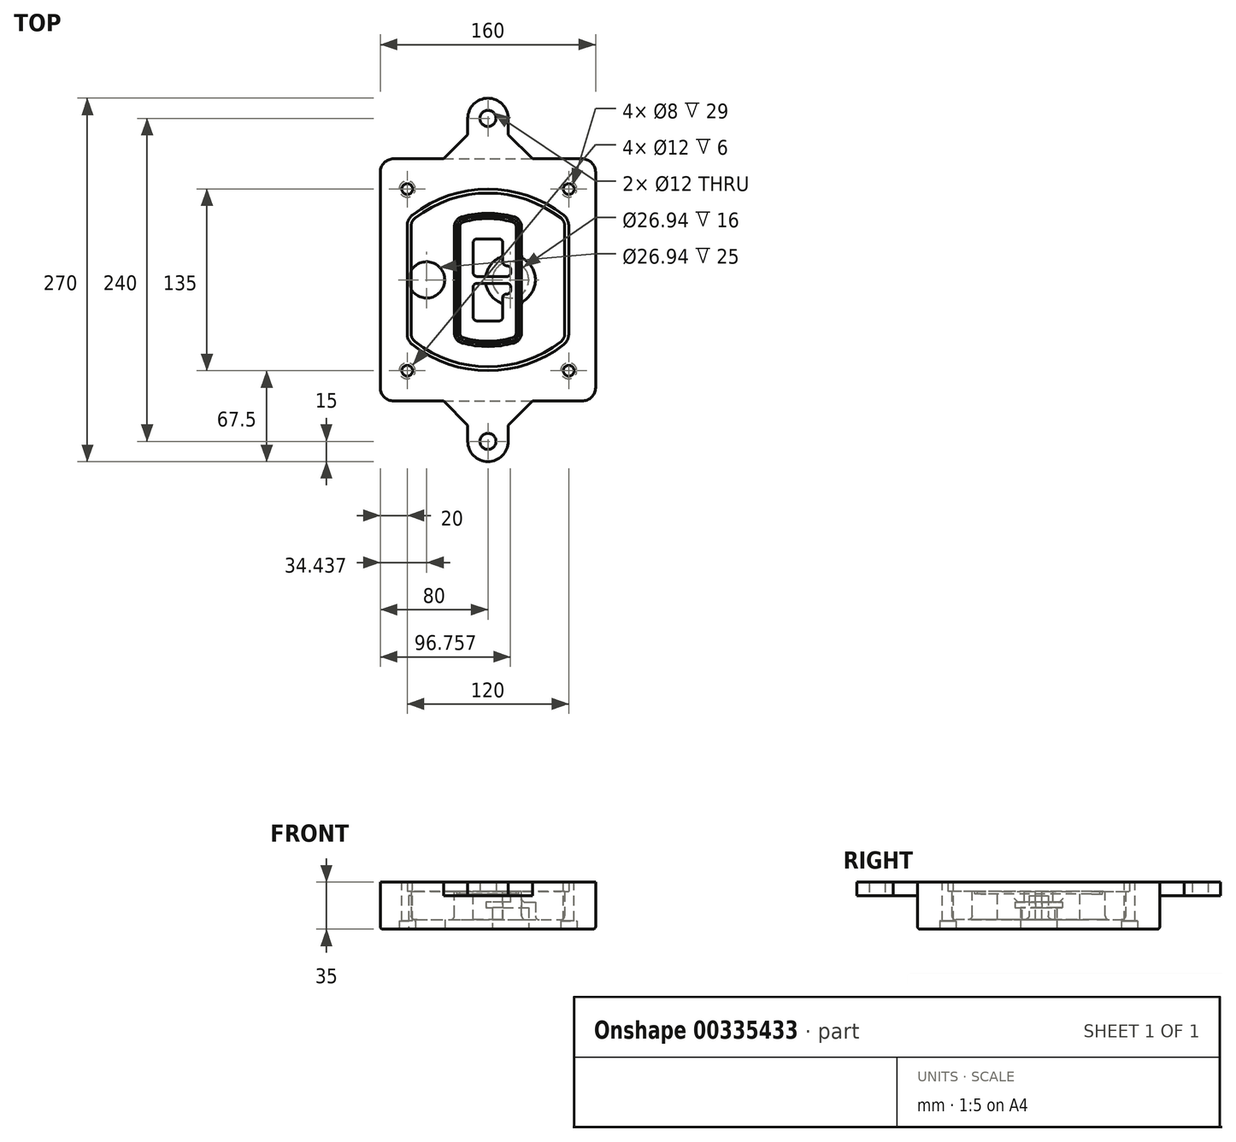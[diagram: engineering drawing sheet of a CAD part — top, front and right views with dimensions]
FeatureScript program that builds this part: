
annotation { "Feature Type Name" : "Feature", "Feature Type Description" : "" }
export const myFeature = defineFeature(function(context is Context, id is Id, definition is map)
    precondition{}
    {
        {
            var Q0;
            Q0=qCreatedBy(makeId("Top.planeOp"),FACE);
            var sketch = newSketch(context, id + "F0", { "sketchPlane" : qUnion([Q0])});
            skPoint(sketch, "E0.rect.middle", {"position": v(0, 0) * mm});
            skLineSegment(sketch, "E1.bottom", {"start": v(-70, -90) * mm, "end": v(70, -90) * mm});
            skLineSegment(sketch, "E1.top", {"start": v(-70, 90) * mm, "end": v(70, 90) * mm});
            skLineSegment(sketch, "E1.left", {"start": v(-80, -80) * mm, "end": v(-80, 80) * mm});
            skLineSegment(sketch, "E1.right", {"start": v(80, -80) * mm, "end": v(80, 80) * mm});
            skLineSegment(sketch, "E2", {"start": v(-80, 90) * mm, "end": v(80, -90) * mm, "construction": true});
            skLineSegment(sketch, "E3", {"start": v(80, 90) * mm, "end": v(-80, -90) * mm, "construction": true});
            skCircle(sketch, "E4", {"center": v(-60, 67.5) * mm, "radius": 4 * mm});
            skCircle(sketch, "E5", {"center": v(60, 67.5) * mm, "radius": 4 * mm});
            skCircle(sketch, "E6", {"center": v(60, -67.5) * mm, "radius": 4 * mm});
            skCircle(sketch, "E7", {"center": v(-60, -67.5) * mm, "radius": 4 * mm});
            skLineSegment(sketch, "E8", {"start": v(-60, 67.5) * mm, "end": v(60, 67.5) * mm, "construction": true});
            skLineSegment(sketch, "E9", {"start": v(60, 67.5) * mm, "end": v(60, -67.5) * mm, "construction": true});
            skLineSegment(sketch, "E10", {"start": v(60, -67.5) * mm, "end": v(-60, -67.5) * mm, "construction": true});
            skLineSegment(sketch, "E11", {"start": v(-60, -67.5) * mm, "end": v(-60, 67.5) * mm, "construction": true});
            skLineSegment(sketch, "E12", {"start": v(-60, 40.3) * mm, "end": v(-60, -40.3) * mm});
            skLineSegment(sketch, "E13", {"start": v(60, 40.3) * mm, "end": v(60, -40.3) * mm});
            skArc(sketch, "E14", {"start": v(56.15, 48.18) * mm, "mid": v(0, 67.5) * mm, "end": v(-56.15, 48.18) * mm});
            skArc(sketch, "E15", {"start": v(-56.15, -48.18) * mm, "mid": v(0, -67.5) * mm, "end": v(56.15, -48.18) * mm});
            skLineSegment(sketch, "E16", {"start": v(-60, 0) * mm, "end": v(60, 0) * mm, "construction": true});
            skPoint(sketch, "E17.visualSharp", {"position": v(-60, -45) * mm});
            skArc(sketch, "E17.filletArc", {"start": v(-60, -40.3) * mm, "mid": v(-58.99, -44.68) * mm, "end": v(-56.15, -48.18) * mm});
            skPoint(sketch, "E18.visualSharp", {"position": v(-60, 45) * mm});
            skArc(sketch, "E18.filletArc", {"start": v(-56.15, 48.18) * mm, "mid": v(-58.99, 44.68) * mm, "end": v(-60, 40.3) * mm});
            skPoint(sketch, "E19.visualSharp", {"position": v(60, 45) * mm});
            skArc(sketch, "E19.filletArc", {"start": v(60, 40.3) * mm, "mid": v(58.99, 44.68) * mm, "end": v(56.15, 48.18) * mm});
            skPoint(sketch, "E20.visualSharp", {"position": v(60, -45) * mm});
            skArc(sketch, "E20.filletArc", {"start": v(56.15, -48.18) * mm, "mid": v(58.99, -44.68) * mm, "end": v(60, -40.3) * mm});
            skPoint(sketch, "E21.visualSharp", {"position": v(-80, 90) * mm});
            skArc(sketch, "E21.filletArc", {"start": v(-70, 90) * mm, "mid": v(-77.07, 87.07) * mm, "end": v(-80, 80) * mm});
            skPoint(sketch, "E22.visualSharp", {"position": v(80, 90) * mm});
            skArc(sketch, "E22.filletArc", {"start": v(80, 80) * mm, "mid": v(77.07, 87.07) * mm, "end": v(70, 90) * mm});
            skPoint(sketch, "E23.visualSharp", {"position": v(80, -90) * mm});
            skArc(sketch, "E23.filletArc", {"start": v(70, -90) * mm, "mid": v(77.07, -87.07) * mm, "end": v(80, -80) * mm});
            skPoint(sketch, "E24.visualSharp", {"position": v(-80, -90) * mm});
            skArc(sketch, "E24.filletArc", {"start": v(-80, -80) * mm, "mid": v(-77.07, -87.07) * mm, "end": v(-70, -90) * mm});
            skArc(sketch, "E25.0", {"start": v(57, 40.3) * mm, "mid": v(56.3, 43.36) * mm, "end": v(54.3, 45.81) * mm});
            skLineSegment(sketch, "E25.1", {"start": v(57, 40.3) * mm, "end": v(57, -40.3) * mm});
            skArc(sketch, "E25.2", {"start": v(54.3, -45.81) * mm, "mid": v(56.3, -43.36) * mm, "end": v(57, -40.3) * mm});
            skArc(sketch, "E25.3", {"start": v(-54.3, -45.81) * mm, "mid": v(0, -64.5) * mm, "end": v(54.3, -45.81) * mm});
            skArc(sketch, "E25.4", {"start": v(-57, -40.3) * mm, "mid": v(-56.3, -43.36) * mm, "end": v(-54.3, -45.81) * mm});
            skArc(sketch, "E25.5", {"start": v(54.3, 45.81) * mm, "mid": v(0, 64.5) * mm, "end": v(-54.3, 45.81) * mm});
            skLineSegment(sketch, "E25.6", {"start": v(-57, 40.3) * mm, "end": v(-57, -40.3) * mm});
            skArc(sketch, "E25.7", {"start": v(-54.3, 45.81) * mm, "mid": v(-56.3, 43.36) * mm, "end": v(-57, 40.3) * mm});
            skArc(sketch, "E26.0", {"start": v(-58.62, 51.33) * mm, "mid": v(-62.58, 46.43) * mm, "end": v(-64, 40.3) * mm});
            skArc(sketch, "E26.1", {"start": v(58.62, 51.33) * mm, "mid": v(0, 71.5) * mm, "end": v(-58.62, 51.33) * mm});
            skArc(sketch, "E26.2", {"start": v(64, 40.3) * mm, "mid": v(62.58, 46.43) * mm, "end": v(58.62, 51.33) * mm});
            skLineSegment(sketch, "E26.3", {"start": v(64, 40.3) * mm, "end": v(64, -40.3) * mm});
            skArc(sketch, "E26.4", {"start": v(58.62, -51.33) * mm, "mid": v(62.58, -46.43) * mm, "end": v(64, -40.3) * mm});
            skLineSegment(sketch, "E26.5", {"start": v(-64, 40.3) * mm, "end": v(-64, -40.3) * mm});
            skArc(sketch, "E26.6", {"start": v(-58.62, -51.33) * mm, "mid": v(0, -71.5) * mm, "end": v(58.62, -51.33) * mm});
            skArc(sketch, "E26.7", {"start": v(-64, -40.3) * mm, "mid": v(-62.58, -46.43) * mm, "end": v(-58.62, -51.33) * mm});
            skSolve(sketch);
        }
        {
            var Q0;
            Q0=makeQuery(id+"F0.imprint","IMPRINT",FACE,{"disambiguationData":[TD([[makeQuery(id+"F0.imprint","IMPRINT",EDGE,{"derivedFrom":sQuery(id+"F0.wireOp",EDGE,"E1.bottom")}),1.0]])]});
            var Q1;
            Q1=makeQuery(id+"F0.imprint","IMPRINT",FACE,{"disambiguationData":[TD([[makeQuery(id+"F0.imprint","IMPRINT",EDGE,{"derivedFrom":sQuery(id+"F0.wireOp",EDGE,"E12")}),1.0]])]});
            var Q2;
            Q2=makeQuery(id+"F0.imprint","IMPRINT",FACE,{"disambiguationData":[TD([[makeQuery(id+"F0.imprint","IMPRINT",EDGE,{"derivedFrom":sQuery(id+"F0.wireOp",EDGE,"E25.0")}),1.0]])]});
            var Q3;
            Q3=makeQuery(id+"F0.imprint","IMPRINT",FACE,{"disambiguationData":[TD([[makeQuery(id+"F0.imprint","IMPRINT",EDGE,{"derivedFrom":sQuery(id+"F0.wireOp",EDGE,"E12")}),-1.0]])]});
            extrude(context, id + "F1", {"entities" : qUnion([Q0, Q1, Q2, Q3]), "oppositeDirection" : true, "depth" : 25 * mm});
        }
        {
            var Q0;
            Q0=makeQuery(id+"F0.imprint","IMPRINT",FACE,{"disambiguationData":[TD([[makeQuery(id+"F0.imprint","IMPRINT",EDGE,{"derivedFrom":sQuery(id+"F0.wireOp",EDGE,"E12")}),1.0]])]});
            extrude(context, id + "F2", {"entities" : qUnion([Q0]), "operationType" : NewBodyOperationType.ADD, "depth" : 3 * mm});
        }
        {
            var Q0;
            Q0=makeQuery(id+"F0.imprint","IMPRINT",FACE,{"disambiguationData":[TD([[makeQuery(id+"F0.imprint","IMPRINT",EDGE,{"derivedFrom":sQuery(id+"F0.wireOp",EDGE,"E25.0")}),1.0]])]});
            extrude(context, id + "F3", {"entities" : qUnion([Q0]), "operationType" : NewBodyOperationType.REMOVE, "oppositeDirection" : true, "depth" : 18 * mm});
        }
        {
            var Q0;
            Q0=makeQuery(id+"F2.opExtrude","CAP_FACE",FACE,{"disambiguationData":[OSD([sQuery(id+"F0.wireOp",EDGE,"E12"),sQuery(id+"F0.wireOp",EDGE,"E13"),sQuery(id+"F0.wireOp",EDGE,"E14"),sQuery(id+"F0.wireOp",EDGE,"E15"),sQuery(id+"F0.wireOp",EDGE,"E17.filletArc"),sQuery(id+"F0.wireOp",EDGE,"E18.filletArc"),sQuery(id+"F0.wireOp",EDGE,"E19.filletArc"),sQuery(id+"F0.wireOp",EDGE,"E20.filletArc"),sQuery(id+"F0.wireOp",EDGE,"E25.0"),sQuery(id+"F0.wireOp",EDGE,"E25.1"),sQuery(id+"F0.wireOp",EDGE,"E25.2"),sQuery(id+"F0.wireOp",EDGE,"E25.3"),sQuery(id+"F0.wireOp",EDGE,"E25.4"),sQuery(id+"F0.wireOp",EDGE,"E25.5"),sQuery(id+"F0.wireOp",EDGE,"E25.6"),sQuery(id+"F0.wireOp",EDGE,"E25.7")])],"isStart":false});
            var sketch = newSketch(context, id + "F4", { "sketchPlane" : qUnion([Q0])});
            skArc(sketch, "E27.0", {"start": v(-19.08, -46.97) * mm, "mid": v(0, -49.5) * mm, "end": v(19.08, -46.97) * mm});
            skArc(sketch, "E28.0", {"start": v(19.08, 46.97) * mm, "mid": v(0, 49.5) * mm, "end": v(-19.08, 46.97) * mm});
            skLineSegment(sketch, "E29", {"start": v(-25, 39.25) * mm, "end": v(-25, -39.25) * mm});
            skLineSegment(sketch, "E30", {"start": v(25, 39.25) * mm, "end": v(25, -39.25) * mm});
            skLineSegment(sketch, "E31", {"start": v(-25, 45.1) * mm, "end": v(25, 45.1) * mm, "construction": true});
            skLineSegment(sketch, "E32", {"start": v(-25, -45.1) * mm, "end": v(25, -45.1) * mm, "construction": true});
            skPoint(sketch, "E33.visualSharp", {"position": v(-25, 45.1) * mm});
            skArc(sketch, "E33.filletArc", {"start": v(-19.08, 46.97) * mm, "mid": v(-23.35, 44.11) * mm, "end": v(-25, 39.25) * mm});
            skPoint(sketch, "E34.visualSharp", {"position": v(25, 45.1) * mm});
            skArc(sketch, "E34.filletArc", {"start": v(25, 39.25) * mm, "mid": v(23.35, 44.11) * mm, "end": v(19.08, 46.97) * mm});
            skPoint(sketch, "E35.visualSharp", {"position": v(25, -45.1) * mm});
            skArc(sketch, "E35.filletArc", {"start": v(19.08, -46.97) * mm, "mid": v(23.35, -44.11) * mm, "end": v(25, -39.25) * mm});
            skPoint(sketch, "E36.visualSharp", {"position": v(-25, -45.1) * mm});
            skArc(sketch, "E36.filletArc", {"start": v(-25, -39.25) * mm, "mid": v(-23.35, -44.11) * mm, "end": v(-19.08, -46.97) * mm});
            skArc(sketch, "E37.0", {"start": v(54.3, 45.81) * mm, "mid": v(0, 64.5) * mm, "end": v(-54.3, 45.81) * mm});
            skArc(sketch, "E37.1", {"start": v(-54.3, 45.81) * mm, "mid": v(-56.3, 43.36) * mm, "end": v(-57, 40.3) * mm});
            skLineSegment(sketch, "E37.2", {"start": v(-57, 40.3) * mm, "end": v(-57, -40.3) * mm});
            skArc(sketch, "E37.3", {"start": v(-57, -40.3) * mm, "mid": v(-56.3, -43.36) * mm, "end": v(-54.3, -45.81) * mm});
            skArc(sketch, "E37.4", {"start": v(-54.3, -45.81) * mm, "mid": v(0, -64.5) * mm, "end": v(54.3, -45.81) * mm});
            skArc(sketch, "E37.5", {"start": v(54.3, -45.81) * mm, "mid": v(56.3, -43.36) * mm, "end": v(57, -40.3) * mm});
            skLineSegment(sketch, "E37.6", {"start": v(57, 40.3) * mm, "end": v(57, -40.3) * mm});
            skArc(sketch, "E37.7", {"start": v(57, 40.3) * mm, "mid": v(56.3, 43.36) * mm, "end": v(54.3, 45.81) * mm});
            skLineSegment(sketch, "E38.0", {"start": v(23, 39.25) * mm, "end": v(23, -39.25) * mm});
            skArc(sketch, "E38.1", {"start": v(18.56, -45.04) * mm, "mid": v(21.76, -42.9) * mm, "end": v(23, -39.25) * mm});
            skArc(sketch, "E38.2", {"start": v(-18.56, -45.04) * mm, "mid": v(0, -47.5) * mm, "end": v(18.56, -45.04) * mm});
            skArc(sketch, "E38.3", {"start": v(-23, -39.25) * mm, "mid": v(-21.76, -42.9) * mm, "end": v(-18.56, -45.04) * mm});
            skLineSegment(sketch, "E38.4", {"start": v(-23, 39.25) * mm, "end": v(-23, -39.25) * mm});
            skArc(sketch, "E38.5", {"start": v(23, 39.25) * mm, "mid": v(21.76, 42.9) * mm, "end": v(18.56, 45.04) * mm});
            skArc(sketch, "E38.6", {"start": v(-18.56, 45.04) * mm, "mid": v(-21.76, 42.9) * mm, "end": v(-23, 39.25) * mm});
            skArc(sketch, "E38.7", {"start": v(18.56, 45.04) * mm, "mid": v(0, 47.5) * mm, "end": v(-18.56, 45.04) * mm});
            skArc(sketch, "E39.0", {"start": v(21, 39.25) * mm, "mid": v(20.18, 41.68) * mm, "end": v(18.04, 43.1) * mm});
            skLineSegment(sketch, "E39.1", {"start": v(21, 39.25) * mm, "end": v(21, -39.25) * mm});
            skArc(sketch, "E39.2", {"start": v(18.04, -43.1) * mm, "mid": v(20.18, -41.68) * mm, "end": v(21, -39.25) * mm});
            skArc(sketch, "E39.3", {"start": v(-18.04, -43.1) * mm, "mid": v(0, -45.5) * mm, "end": v(18.04, -43.1) * mm});
            skArc(sketch, "E39.4", {"start": v(-21, -39.25) * mm, "mid": v(-20.18, -41.68) * mm, "end": v(-18.04, -43.1) * mm});
            skArc(sketch, "E39.5", {"start": v(18.04, 43.1) * mm, "mid": v(0, 45.5) * mm, "end": v(-18.04, 43.1) * mm});
            skLineSegment(sketch, "E39.6", {"start": v(-21, 39.25) * mm, "end": v(-21, -39.25) * mm});
            skArc(sketch, "E39.7", {"start": v(-18.04, 43.1) * mm, "mid": v(-20.18, 41.68) * mm, "end": v(-21, 39.25) * mm});
            skLineSegment(sketch, "E40", {"start": v(-25, 0) * mm, "end": v(25, 0) * mm, "construction": true});
            skLineSegment(sketch, "E41", {"start": v(-11, 5.5) * mm, "end": v(-11, 27.5) * mm});
            skLineSegment(sketch, "E42", {"start": v(-8, 30.5) * mm, "end": v(8, 30.5) * mm});
            skLineSegment(sketch, "E43", {"start": v(11, 27.5) * mm, "end": v(11, 13.5) * mm});
            skLineSegment(sketch, "E44", {"start": v(14, 10.5) * mm, "end": v(14, 10.5) * mm});
            skLineSegment(sketch, "E45", {"start": v(17, 7.5) * mm, "end": v(17, 5.5) * mm});
            skLineSegment(sketch, "E46", {"start": v(14, 2.5) * mm, "end": v(-8, 2.5) * mm});
            skPoint(sketch, "E47.visualSharp", {"position": v(-11, 30.5) * mm});
            skArc(sketch, "E47.filletArc", {"start": v(-8, 30.5) * mm, "mid": v(-10.12, 29.62) * mm, "end": v(-11, 27.5) * mm});
            skPoint(sketch, "E48.visualSharp", {"position": v(11, 30.5) * mm});
            skArc(sketch, "E48.filletArc", {"start": v(11, 27.5) * mm, "mid": v(10.12, 29.62) * mm, "end": v(8, 30.5) * mm});
            skPoint(sketch, "E49.visualSharp", {"position": v(11, 10.5) * mm});
            skArc(sketch, "E49.filletArc", {"start": v(11, 13.5) * mm, "mid": v(11.88, 11.38) * mm, "end": v(14, 10.5) * mm});
            skPoint(sketch, "E50.visualSharp", {"position": v(17, 10.5) * mm});
            skArc(sketch, "E50.filletArc", {"start": v(17, 7.5) * mm, "mid": v(16.12, 9.62) * mm, "end": v(14, 10.5) * mm});
            skPoint(sketch, "E51.visualSharp", {"position": v(17, 2.5) * mm});
            skArc(sketch, "E51.filletArc", {"start": v(14, 2.5) * mm, "mid": v(16.12, 3.38) * mm, "end": v(17, 5.5) * mm});
            skPoint(sketch, "E52.visualSharp", {"position": v(-11, 2.5) * mm});
            skArc(sketch, "E52.filletArc", {"start": v(-11, 5.5) * mm, "mid": v(-10.12, 3.38) * mm, "end": v(-8, 2.5) * mm});
            skLineSegment(sketch, "E53.0.MirrorCS", {"start": v(14, -2.5) * mm, "end": v(-8, -2.5) * mm});
            skArc(sketch, "E54.0.MirrorCS", {"start": v(-11, -5.5) * mm, "mid": v(-10.12, -3.38) * mm, "end": v(-8, -2.5) * mm});
            skLineSegment(sketch, "E55.0.MirrorCS", {"start": v(-11, -5.5) * mm, "end": v(-11, -27.5) * mm});
            skArc(sketch, "E56.0.MirrorCS", {"start": v(-8, -30.5) * mm, "mid": v(-10.12, -29.62) * mm, "end": v(-11, -27.5) * mm});
            skLineSegment(sketch, "E57.0.MirrorCS", {"start": v(-8, -30.5) * mm, "end": v(8, -30.5) * mm});
            skArc(sketch, "E58.0.MirrorCS", {"start": v(11, -27.5) * mm, "mid": v(10.12, -29.62) * mm, "end": v(8, -30.5) * mm});
            skLineSegment(sketch, "E59.0.MirrorCS", {"start": v(11, -27.5) * mm, "end": v(11, -13.5) * mm});
            skArc(sketch, "E60.0.MirrorCS", {"start": v(11, -13.5) * mm, "mid": v(11.88, -11.38) * mm, "end": v(14, -10.5) * mm});
            skArc(sketch, "E61.0.MirrorCS", {"start": v(17, -7.5) * mm, "mid": v(16.12, -9.62) * mm, "end": v(14, -10.5) * mm});
            skLineSegment(sketch, "E62.0.MirrorCS", {"start": v(17, -7.5) * mm, "end": v(17, -5.5) * mm});
            skArc(sketch, "E63.0.MirrorCS", {"start": v(14, -2.5) * mm, "mid": v(16.12, -3.38) * mm, "end": v(17, -5.5) * mm});
            skSolve(sketch);
        }
        {
            var Q0;
            Q0=makeQuery(id+"F4.imprint","IMPRINT",FACE,{"disambiguationData":[TD([[makeQuery(id+"F4.imprint","IMPRINT",EDGE,{"derivedFrom":sQuery(id+"F4.wireOp",EDGE,"E27.0")}),1.0]])]});
            var Q1;
            Q1=makeQuery(id+"F4.imprint","IMPRINT",FACE,{"disambiguationData":[TD([[makeQuery(id+"F4.imprint","IMPRINT",EDGE,{"derivedFrom":sQuery(id+"F4.wireOp",EDGE,"E38.0")}),-1.0]])]});
            var Q2;
            Q2=makeQuery(id+"F4.imprint","IMPRINT",FACE,{"disambiguationData":[TD([[makeQuery(id+"F4.imprint","IMPRINT",EDGE,{"derivedFrom":sQuery(id+"F4.wireOp",EDGE,"E39.0")}),1.0]])]});
            extrude(context, id + "F5", {"entities" : qUnion([Q0, Q1, Q2]), "operationType" : NewBodyOperationType.ADD, "endBound" : BoundingType.UP_TO_NEXT, "oppositeDirection" : true, "depth" : 25 * mm});
        }
        {
            var Q0;
            Q0=makeQuery(id+"F4.imprint","IMPRINT",FACE,{"disambiguationData":[TD([[makeQuery(id+"F4.imprint","IMPRINT",EDGE,{"derivedFrom":sQuery(id+"F4.wireOp",EDGE,"E38.0")}),-1.0]])]});
            extrude(context, id + "F6", {"entities" : qUnion([Q0]), "operationType" : NewBodyOperationType.REMOVE, "oppositeDirection" : true, "depth" : 2 * mm});
        }
        {
            var Q0;
            Q0=makeQuery(id+"F1.opExtrude","CAP_FACE",FACE,{"disambiguationData":[OSD([sQuery(id+"F0.wireOp",EDGE,"E1.bottom"),sQuery(id+"F0.wireOp",EDGE,"E1.top"),sQuery(id+"F0.wireOp",EDGE,"E1.left"),sQuery(id+"F0.wireOp",EDGE,"E1.right"),sQuery(id+"F0.wireOp",EDGE,"E4"),sQuery(id+"F0.wireOp",EDGE,"E5"),sQuery(id+"F0.wireOp",EDGE,"E6"),sQuery(id+"F0.wireOp",EDGE,"E7"),sQuery(id+"F0.wireOp",EDGE,"E21.filletArc"),sQuery(id+"F0.wireOp",EDGE,"E22.filletArc"),sQuery(id+"F0.wireOp",EDGE,"E23.filletArc"),sQuery(id+"F0.wireOp",EDGE,"E24.filletArc")])],"isStart":false});
            var sketch = newSketch(context, id + "F7", { "sketchPlane" : qUnion([Q0])});
            skCircle(sketch, "E64", {"center": v(16.76, 0) * mm, "radius": 13.47 * mm});
            skCircle(sketch, "E65", {"center": v(-45.56, 0) * mm, "radius": 13.47 * mm});
            skLineSegment(sketch, "E66", {"start": v(80, 0) * mm, "end": v(-80, 0) * mm});
            skCircle(sketch, "E67", {"center": v(16.76, 0) * mm, "radius": 18.47 * mm});
            skCircle(sketch, "E68", {"center": v(60, -67.5) * mm, "radius": 6 * mm});
            skCircle(sketch, "E69", {"center": v(-60, -67.5) * mm, "radius": 6 * mm});
            skCircle(sketch, "E70", {"center": v(-60, 67.5) * mm, "radius": 6 * mm});
            skCircle(sketch, "E71", {"center": v(60, 67.5) * mm, "radius": 6 * mm});
            skSolve(sketch);
        }
        {
            var Q0;
            {var subQ1=sQuery(id+"F7.wireOp",EDGE,"E66");var subQ4=sQuery(id+"F7.wireOp",EDGE,"E64");var subQ6=makeQuery(id+"F7.imprint","INTERSECT",VERTEX,{"disambiguationData":[OD(0.0)],"derivedFrom":[subQ4,subQ1]});Q0=makeQuery(id+"F7.imprint","IMPRINT",FACE,{"disambiguationData":[TD([[makeQuery(id+"F7.imprint","IMPRINT",EDGE,{"disambiguationData":[TD([[subQ6,-1.0]])],"derivedFrom":subQ4}),-1.0]])]});}
            var Q1;
            {var subQ0=sQuery(id+"F7.wireOp",EDGE,"E66");var subQ1=sQuery(id+"F7.wireOp",EDGE,"E64");var subQ3=makeQuery(id+"F7.imprint","INTERSECT",VERTEX,{"disambiguationData":[OD(0.0)],"derivedFrom":[subQ1,subQ0]});Q1=makeQuery(id+"F7.imprint","IMPRINT",FACE,{"disambiguationData":[TD([[makeQuery(id+"F7.imprint","IMPRINT",EDGE,{"disambiguationData":[TD([[subQ3,-1.0]])],"derivedFrom":subQ1}),1.0]])]});}
            var Q2;
            {var subQ0=sQuery(id+"F7.wireOp",EDGE,"E66");var subQ1=sQuery(id+"F7.wireOp",EDGE,"E64");var subQ3=makeQuery(id+"F7.imprint","INTERSECT",VERTEX,{"disambiguationData":[OD(0.0)],"derivedFrom":[subQ1,subQ0]});Q2=makeQuery(id+"F7.imprint","IMPRINT",FACE,{"disambiguationData":[TD([[makeQuery(id+"F7.imprint","IMPRINT",EDGE,{"disambiguationData":[TD([[subQ3,1.0]])],"derivedFrom":subQ1}),1.0]])]});}
            var Q3;
            {var subQ1=sQuery(id+"F7.wireOp",EDGE,"E66");var subQ4=sQuery(id+"F7.wireOp",EDGE,"E64");var subQ6=makeQuery(id+"F7.imprint","INTERSECT",VERTEX,{"disambiguationData":[OD(0.0)],"derivedFrom":[subQ4,subQ1]});Q3=makeQuery(id+"F7.imprint","IMPRINT",FACE,{"disambiguationData":[TD([[makeQuery(id+"F7.imprint","IMPRINT",EDGE,{"disambiguationData":[TD([[subQ6,1.0]])],"derivedFrom":subQ4}),-1.0]])]});}
            extrude(context, id + "F8", {"entities" : qUnion([Q0, Q1, Q2, Q3]), "operationType" : NewBodyOperationType.ADD, "oppositeDirection" : true, "depth" : 20 * mm});
        }
        {
            var Q0;
            {var subQ0=sQuery(id+"F7.wireOp",EDGE,"E66");var subQ1=sQuery(id+"F7.wireOp",EDGE,"E64");var subQ3=makeQuery(id+"F7.imprint","INTERSECT",VERTEX,{"disambiguationData":[OD(0.0)],"derivedFrom":[subQ1,subQ0]});Q0=makeQuery(id+"F7.imprint","IMPRINT",FACE,{"disambiguationData":[TD([[makeQuery(id+"F7.imprint","IMPRINT",EDGE,{"disambiguationData":[TD([[subQ3,-1.0]])],"derivedFrom":subQ1}),1.0]])]});}
            var Q1;
            {var subQ0=sQuery(id+"F7.wireOp",EDGE,"E66");var subQ1=sQuery(id+"F7.wireOp",EDGE,"E64");var subQ3=makeQuery(id+"F7.imprint","INTERSECT",VERTEX,{"disambiguationData":[OD(0.0)],"derivedFrom":[subQ1,subQ0]});Q1=makeQuery(id+"F7.imprint","IMPRINT",FACE,{"disambiguationData":[TD([[makeQuery(id+"F7.imprint","IMPRINT",EDGE,{"disambiguationData":[TD([[subQ3,1.0]])],"derivedFrom":subQ1}),1.0]])]});}
            extrude(context, id + "F9", {"entities" : qUnion([Q0, Q1]), "operationType" : NewBodyOperationType.REMOVE, "oppositeDirection" : true, "depth" : 16 * mm});
        }
        {
            var Q0;
            {var subQ0=sQuery(id+"F7.wireOp",EDGE,"E66");var subQ1=sQuery(id+"F7.wireOp",EDGE,"E65");var subQ3=makeQuery(id+"F7.imprint","INTERSECT",VERTEX,{"disambiguationData":[OD(0.0)],"derivedFrom":[subQ1,subQ0]});Q0=makeQuery(id+"F7.imprint","IMPRINT",FACE,{"disambiguationData":[TD([[makeQuery(id+"F7.imprint","IMPRINT",EDGE,{"disambiguationData":[TD([[subQ3,-1.0]])],"derivedFrom":subQ1}),1.0]])]});}
            var Q1;
            {var subQ0=sQuery(id+"F7.wireOp",EDGE,"E66");var subQ1=sQuery(id+"F7.wireOp",EDGE,"E65");var subQ3=makeQuery(id+"F7.imprint","INTERSECT",VERTEX,{"disambiguationData":[OD(0.0)],"derivedFrom":[subQ1,subQ0]});Q1=makeQuery(id+"F7.imprint","IMPRINT",FACE,{"disambiguationData":[TD([[makeQuery(id+"F7.imprint","IMPRINT",EDGE,{"disambiguationData":[TD([[subQ3,1.0]])],"derivedFrom":subQ1}),1.0]])]});}
            extrude(context, id + "F10", {"entities" : qUnion([Q0, Q1]), "operationType" : NewBodyOperationType.REMOVE, "oppositeDirection" : true, "depth" : 25 * mm});
        }
        {
            var Q0;
            Q0=makeQuery(id+"F7.imprint","IMPRINT",FACE,{"disambiguationData":[TD([[makeQuery(id+"F7.imprint","IMPRINT",EDGE,{"derivedFrom":sQuery(id+"F7.wireOp",EDGE,"E68")}),1.0]])]});
            var Q1;
            Q1=makeQuery(id+"F7.imprint","IMPRINT",FACE,{"disambiguationData":[TD([[makeQuery(id+"F7.imprint","IMPRINT",EDGE,{"derivedFrom":makeQuery(id+"F1.opExtrude","CAP_EDGE",EDGE,{"disambiguationData":[OSD([sQuery(id+"F0.wireOp",EDGE,"E5")])],"isStart":false})}),-1.0]])]});
            var Q2;
            Q2=makeQuery(id+"F7.imprint","IMPRINT",FACE,{"disambiguationData":[TD([[makeQuery(id+"F7.imprint","IMPRINT",EDGE,{"derivedFrom":sQuery(id+"F7.wireOp",EDGE,"E69")}),1.0]])]});
            var Q3;
            Q3=makeQuery(id+"F7.imprint","IMPRINT",FACE,{"disambiguationData":[TD([[makeQuery(id+"F7.imprint","IMPRINT",EDGE,{"derivedFrom":makeQuery(id+"F1.opExtrude","CAP_EDGE",EDGE,{"disambiguationData":[OSD([sQuery(id+"F0.wireOp",EDGE,"E4")])],"isStart":false})}),-1.0]])]});
            var Q4;
            Q4=makeQuery(id+"F7.imprint","IMPRINT",FACE,{"disambiguationData":[TD([[makeQuery(id+"F7.imprint","IMPRINT",EDGE,{"derivedFrom":sQuery(id+"F7.wireOp",EDGE,"E70")}),1.0]])]});
            var Q5;
            Q5=makeQuery(id+"F7.imprint","IMPRINT",FACE,{"disambiguationData":[TD([[makeQuery(id+"F7.imprint","IMPRINT",EDGE,{"derivedFrom":makeQuery(id+"F1.opExtrude","CAP_EDGE",EDGE,{"disambiguationData":[OSD([sQuery(id+"F0.wireOp",EDGE,"E7")])],"isStart":false})}),-1.0]])]});
            var Q6;
            Q6=makeQuery(id+"F7.imprint","IMPRINT",FACE,{"disambiguationData":[TD([[makeQuery(id+"F7.imprint","IMPRINT",EDGE,{"derivedFrom":sQuery(id+"F7.wireOp",EDGE,"E71")}),1.0]])]});
            var Q7;
            Q7=makeQuery(id+"F7.imprint","IMPRINT",FACE,{"disambiguationData":[TD([[makeQuery(id+"F7.imprint","IMPRINT",EDGE,{"derivedFrom":makeQuery(id+"F1.opExtrude","CAP_EDGE",EDGE,{"disambiguationData":[OSD([sQuery(id+"F0.wireOp",EDGE,"E6")])],"isStart":false})}),-1.0]])]});
            extrude(context, id + "F11", {"entities" : qUnion([Q0, Q1, Q2, Q3, Q4, Q5, Q6, Q7]), "operationType" : NewBodyOperationType.REMOVE, "oppositeDirection" : true, "depth" : 6 * mm});
        }
        {
            var Q0;
            Q0=makeQuery(id+"F9.boolean.opBoolean","COPY",FACE,{"derivedFrom":makeQuery(id+"F9.opExtrude","CAP_FACE",FACE,{"disambiguationData":[OSD([sQuery(id+"F7.wireOp",EDGE,"E64")])],"isStart":false})});
            var sketch = newSketch(context, id + "F12", { "sketchPlane" : qUnion([Q0])});
            skArc(sketch, "E72.0", {"start": v(11, 17.55) * mm, "mid": v(2.57, 11.82) * mm, "end": v(-1.54, 2.5) * mm});
            skArc(sketch, "E72.1", {"start": v(-1.54, -2.5) * mm, "mid": v(2.57, -11.82) * mm, "end": v(11, -17.55) * mm});
            skLineSegment(sketch, "E73", {"start": v(-1.54, -2.5) * mm, "end": v(14, -2.5) * mm});
            skLineSegment(sketch, "E74.0", {"start": v(14, 2.5) * mm, "end": v(-1.54, 2.5) * mm});
            skArc(sketch, "E74.1", {"start": v(14, 2.5) * mm, "mid": v(16.12, 3.38) * mm, "end": v(17, 5.5) * mm});
            skLineSegment(sketch, "E74.2", {"start": v(17, 7.5) * mm, "end": v(17, 5.5) * mm});
            skArc(sketch, "E74.3", {"start": v(17, 7.5) * mm, "mid": v(16.12, 9.62) * mm, "end": v(14, 10.5) * mm});
            skArc(sketch, "E74.4", {"start": v(11, 13.5) * mm, "mid": v(11.88, 11.38) * mm, "end": v(14, 10.5) * mm});
            skLineSegment(sketch, "E74.5", {"start": v(11, 17.55) * mm, "end": v(11, 13.5) * mm});
            skLineSegment(sketch, "E74.7", {"start": v(14, -2.5) * mm, "end": v(-1.54, -2.5) * mm});
            skArc(sketch, "E74.8", {"start": v(14, -2.5) * mm, "mid": v(16.12, -3.38) * mm, "end": v(17, -5.5) * mm});
            skLineSegment(sketch, "E74.9", {"start": v(17, -7.5) * mm, "end": v(17, -5.5) * mm});
            skArc(sketch, "E74.10", {"start": v(17, -7.5) * mm, "mid": v(16.12, -9.62) * mm, "end": v(14, -10.5) * mm});
            skArc(sketch, "E74.11", {"start": v(11, -13.5) * mm, "mid": v(11.88, -11.38) * mm, "end": v(14, -10.5) * mm});
            skLineSegment(sketch, "E74.12", {"start": v(11, -17.55) * mm, "end": v(11, -13.5) * mm});
            skPoint(sketch, "E75.orphan", {"position": v(11, -27.5) * mm});
            skPoint(sketch, "E76.orphan", {"position": v(-8, -2.5) * mm});
            skPoint(sketch, "E77.orphan", {"position": v(-8, 2.5) * mm});
            skPoint(sketch, "E78.orphan", {"position": v(11, 27.5) * mm});
            skSolve(sketch);
        }
        {
            var Q0;
            {var subQ7=sQuery(id+"F12.wireOp",EDGE,"E72.0");var subQ14=sQuery(id+"F12.wireOp",EDGE,"E72.1");var subQ16=sQuery(id+"F12.wireOp",EDGE,"E74.1");var subQ18=sQuery(id+"F12.wireOp",EDGE,"E74.8");Q0=qUnion([makeQuery(id+"F12.imprint","IMPRINT",FACE,{"disambiguationData":[TD([[makeQuery(id+"F12.imprint","IMPRINT",EDGE,{"derivedFrom":subQ7}),1.0]])]}),makeQuery(id+"F12.imprint","IMPRINT",FACE,{"disambiguationData":[TD([[makeQuery(id+"F12.imprint","IMPRINT",EDGE,{"derivedFrom":subQ14}),1.0]])]}),makeQuery(id+"F12.imprint","IMPRINT",FACE,{"disambiguationData":[TD([[makeQuery(id+"F12.imprint","IMPRINT",EDGE,{"derivedFrom":subQ16}),1.0]])]}),makeQuery(id+"F12.imprint","IMPRINT",FACE,{"disambiguationData":[TD([[makeQuery(id+"F12.imprint","IMPRINT",EDGE,{"derivedFrom":subQ18}),-1.0]])]})]);}
            var Q1;
            Q1=makeQuery(id+"F5.boolean.opBoolean","SPLIT",FACE,{"disambiguationData":[TD([makeQuery(id+"F5.opExtrude","SWEPT_FACE",FACE,{"disambiguationData":[OSD([sQuery(id+"F4.wireOp",EDGE,"E41")])]})])],"derivedFrom":makeQuery(id+"F3.boolean.opBoolean","COPY",FACE,{"derivedFrom":makeQuery(id+"F3.opExtrude","CAP_FACE",FACE,{"disambiguationData":[OSD([sQuery(id+"F0.wireOp",EDGE,"E25.0"),sQuery(id+"F0.wireOp",EDGE,"E25.1"),sQuery(id+"F0.wireOp",EDGE,"E25.2"),sQuery(id+"F0.wireOp",EDGE,"E25.3"),sQuery(id+"F0.wireOp",EDGE,"E25.4"),sQuery(id+"F0.wireOp",EDGE,"E25.5"),sQuery(id+"F0.wireOp",EDGE,"E25.6"),sQuery(id+"F0.wireOp",EDGE,"E25.7")])],"isStart":false})})});
            extrude(context, id + "F13", {"entities" : qUnion([Q0]), "operationType" : NewBodyOperationType.REMOVE, "endBound" : BoundingType.UP_TO_SURFACE, "endBoundEntityFace" : qUnion([Q1]), "depth" : 25 * mm});
        }
        {
            var Q0;
            Q0=makeQuery(id+"F3.boolean.opBoolean","COPY",EDGE,{"derivedFrom":makeQuery(id+"F3.opExtrude","CAP_EDGE",EDGE,{"disambiguationData":[OSD([sQuery(id+"F0.wireOp",EDGE,"E25.6")])],"isStart":false})});
            var Q1;
            Q1=makeQuery(id+"F8.boolean.opBoolean","INTERSECT",EDGE,{"derivedFrom":[makeQuery(id+"F5.opExtrude","SWEPT_FACE",FACE,{"disambiguationData":[OSD([sQuery(id+"F4.wireOp",EDGE,"E30")])]}),makeQuery(id+"F8.opExtrude","CAP_FACE",FACE,{"disambiguationData":[OSD([sQuery(id+"F7.wireOp",EDGE,"E67")])],"isStart":false})]});
            var Q2;
            Q2=makeQuery(id+"F8.boolean.opBoolean","INTERSECT",EDGE,{"disambiguationData":[OD(1.0)],"derivedFrom":[makeQuery(id+"F5.opExtrude","SWEPT_FACE",FACE,{"disambiguationData":[OSD([sQuery(id+"F4.wireOp",EDGE,"E30")])]}),makeQuery(id+"F8.opExtrude","SWEPT_FACE",FACE,{"disambiguationData":[OSD([sQuery(id+"F7.wireOp",EDGE,"E67")])]})]});
            var Q3;
            {var subQ0=sQuery(id+"F4.wireOp",EDGE,"E30");Q3=makeQuery(id+"F8.boolean.opBoolean","SPLIT",EDGE,{"disambiguationData":[TD([makeQuery(id+"F5.opExtrude","SWEPT_FACE",FACE,{"disambiguationData":[OSD([sQuery(id+"F4.wireOp",EDGE,"E35.filletArc")])]})])],"derivedFrom":makeQuery(id+"F5.opExtrude","CAP_EDGE",EDGE,{"disambiguationData":[OSD([subQ0])],"isStart":false})});}
            var Q4;
            {var subQ0=sQuery(id+"F0.wireOp",EDGE,"E25.7");var subQ1=sQuery(id+"F0.wireOp",EDGE,"E25.1");var subQ2=sQuery(id+"F0.wireOp",EDGE,"E25.6");var subQ3=sQuery(id+"F0.wireOp",EDGE,"E25.5");var subQ4=sQuery(id+"F0.wireOp",EDGE,"E25.4");var subQ5=sQuery(id+"F0.wireOp",EDGE,"E25.0");var subQ6=sQuery(id+"F0.wireOp",EDGE,"E25.2");var subQ7=sQuery(id+"F0.wireOp",EDGE,"E25.3");Q4=makeQuery(id+"F8.boolean.opBoolean","INTERSECT",EDGE,{"derivedFrom":[makeQuery(id+"F5.boolean.opBoolean","SPLIT",FACE,{"disambiguationData":[TD([makeQuery(id+"F2.opExtrude","SWEPT_FACE",FACE,{"disambiguationData":[OSD([subQ5])]})])],"derivedFrom":makeQuery(id+"F3.boolean.opBoolean","COPY",FACE,{"derivedFrom":makeQuery(id+"F3.opExtrude","CAP_FACE",FACE,{"disambiguationData":[OSD([subQ5,subQ1,subQ6,subQ7,subQ4,subQ3,subQ2,subQ0])],"isStart":false})})}),makeQuery(id+"F8.opExtrude","SWEPT_FACE",FACE,{"disambiguationData":[OSD([sQuery(id+"F7.wireOp",EDGE,"E67")])]})]});}
            var Q5;
            Q5=makeQuery(id+"F8.boolean.opBoolean","INTERSECT",EDGE,{"disambiguationData":[OD(0.0)],"derivedFrom":[makeQuery(id+"F5.opExtrude","SWEPT_FACE",FACE,{"disambiguationData":[OSD([sQuery(id+"F4.wireOp",EDGE,"E30")])]}),makeQuery(id+"F8.opExtrude","SWEPT_FACE",FACE,{"disambiguationData":[OSD([sQuery(id+"F7.wireOp",EDGE,"E67")])]})]});
            fillet(context, id + "F14", {"entities" : qUnion([Q0, Q1, Q2, Q3, Q4, Q5]), "radius" : 3 * mm, "tangentPropagation" : true, "allowEdgeOverflow" : false});
        }
        {
            var Q0;
            Q0=makeQuery(id+"F1.opExtrude","CAP_EDGE",EDGE,{"disambiguationData":[OSD([sQuery(id+"F0.wireOp",EDGE,"E1.bottom")])],"isStart":false});
            fillet(context, id + "F15", {"entities" : qUnion([Q0]), "radius" : 2 * mm, "tangentPropagation" : true, "allowEdgeOverflow" : false});
        }
        {
            var Q0;
            {var subQ0=sQuery(id+"F0.wireOp",EDGE,"E21.filletArc");var subQ1=sQuery(id+"F0.wireOp",EDGE,"E7");var subQ2=sQuery(id+"F0.wireOp",EDGE,"E6");var subQ3=sQuery(id+"F0.wireOp",EDGE,"E5");var subQ4=sQuery(id+"F0.wireOp",EDGE,"E4");var subQ5=sQuery(id+"F0.wireOp",EDGE,"E22.filletArc");var subQ6=sQuery(id+"F0.wireOp",EDGE,"E1.bottom");var subQ7=sQuery(id+"F0.wireOp",EDGE,"E1.right");var subQ8=sQuery(id+"F0.wireOp",EDGE,"E1.top");var subQ9=sQuery(id+"F0.wireOp",EDGE,"E1.left");var subQ10=sQuery(id+"F0.wireOp",EDGE,"E23.filletArc");var subQ11=sQuery(id+"F0.wireOp",EDGE,"E24.filletArc");Q0=makeQuery(id+"F2.boolean.opBoolean","SPLIT",FACE,{"disambiguationData":[TD([makeQuery(id+"F1.opExtrude","SWEPT_FACE",FACE,{"disambiguationData":[OSD([subQ6])]})])],"derivedFrom":makeQuery(id+"F1.opExtrude","CAP_FACE",FACE,{"disambiguationData":[OSD([subQ6,subQ8,subQ9,subQ7,subQ4,subQ3,subQ2,subQ1,subQ0,subQ5,subQ10,subQ11])],"isStart":true})});}
            var sketch = newSketch(context, id + "F16", { "sketchPlane" : qUnion([Q0])});
            skCircle(sketch, "E79", {"center": v(0, 120) * mm, "radius": 6 * mm});
            skArc(sketch, "E80", {"start": v(15, 120) * mm, "mid": v(0, 135) * mm, "end": v(-15, 120) * mm});
            skLineSegment(sketch, "E81", {"start": v(0, 120) * mm, "end": v(0, 90) * mm, "construction": true});
            skLineSegment(sketch, "E82", {"start": v(-15, 120) * mm, "end": v(-15, 108) * mm});
            skLineSegment(sketch, "E83", {"start": v(15, 120) * mm, "end": v(15, 108) * mm});
            skLineSegment(sketch, "E84", {"start": v(-74.67, 0) * mm, "end": v(74.28, 0) * mm, "construction": true});
            skLineSegment(sketch, "E85", {"start": v(15, 108) * mm, "end": v(33, 90) * mm});
            skLineSegment(sketch, "E86", {"start": v(-15, 108) * mm, "end": v(-33, 90) * mm});
            skArc(sketch, "E87.MirrorCS", {"start": v(-15, 120) * mm, "mid": v(0, 135) * mm, "end": v(15, 120) * mm});
            skLineSegment(sketch, "E88.MirrorCS", {"start": v(74.67, 0) * mm, "end": v(-74.28, 0) * mm, "construction": true});
            skLineSegment(sketch, "E89.MirrorCS", {"start": v(-15, -120) * mm, "end": v(-15, -108) * mm});
            skLineSegment(sketch, "E90.MirrorCS", {"start": v(-15, -108) * mm, "end": v(-33, -90) * mm});
            skLineSegment(sketch, "E91.MirrorCS", {"start": v(15, -108) * mm, "end": v(33, -90) * mm});
            skLineSegment(sketch, "E92.MirrorCS", {"start": v(15, -120) * mm, "end": v(15, -108) * mm});
            skArc(sketch, "E93.MirrorCS", {"start": v(15, -120) * mm, "mid": v(0, -135) * mm, "end": v(-15, -120) * mm});
            skLineSegment(sketch, "E94.MirrorCS", {"start": v(0, -120) * mm, "end": v(0, -90) * mm, "construction": true});
            skCircle(sketch, "E95.MirrorC", {"center": v(0, -120) * mm, "radius": 6 * mm});
            skSolve(sketch);
        }
        {
            var Q0;
            Q0=makeQuery(id+"F16.imprint","IMPRINT",FACE,{"disambiguationData":[TD([[makeQuery(id+"F16.imprint","IMPRINT",EDGE,{"derivedFrom":makeQuery(id+"F1.opExtrude","CAP_EDGE",EDGE,{"disambiguationData":[OSD([sQuery(id+"F0.wireOp",EDGE,"E1.left")])],"isStart":true})}),-1.0]])]});
            var Q1;
            Q1=makeQuery(id+"F16.imprint","IMPRINT",FACE,{"disambiguationData":[TD([[makeQuery(id+"F16.imprint","IMPRINT",EDGE,{"derivedFrom":sQuery(id+"F16.wireOp",EDGE,"E82")}),1.0]])]});
            var Q2;
            {var subQ0=sQuery(id+"F16.wireOp",EDGE,"E91.MirrorCS");Q2=makeQuery(id+"F16.imprint","IMPRINT",FACE,{"disambiguationData":[TD([[makeQuery(id+"F16.imprint","IMPRINT",EDGE,{"derivedFrom":subQ0}),1.0]])]});}
            extrude(context, id + "F17", {"entities" : qUnion([Q0, Q1, Q2]), "operationType" : NewBodyOperationType.ADD, "depth" : 10 * mm});
        }
    });
